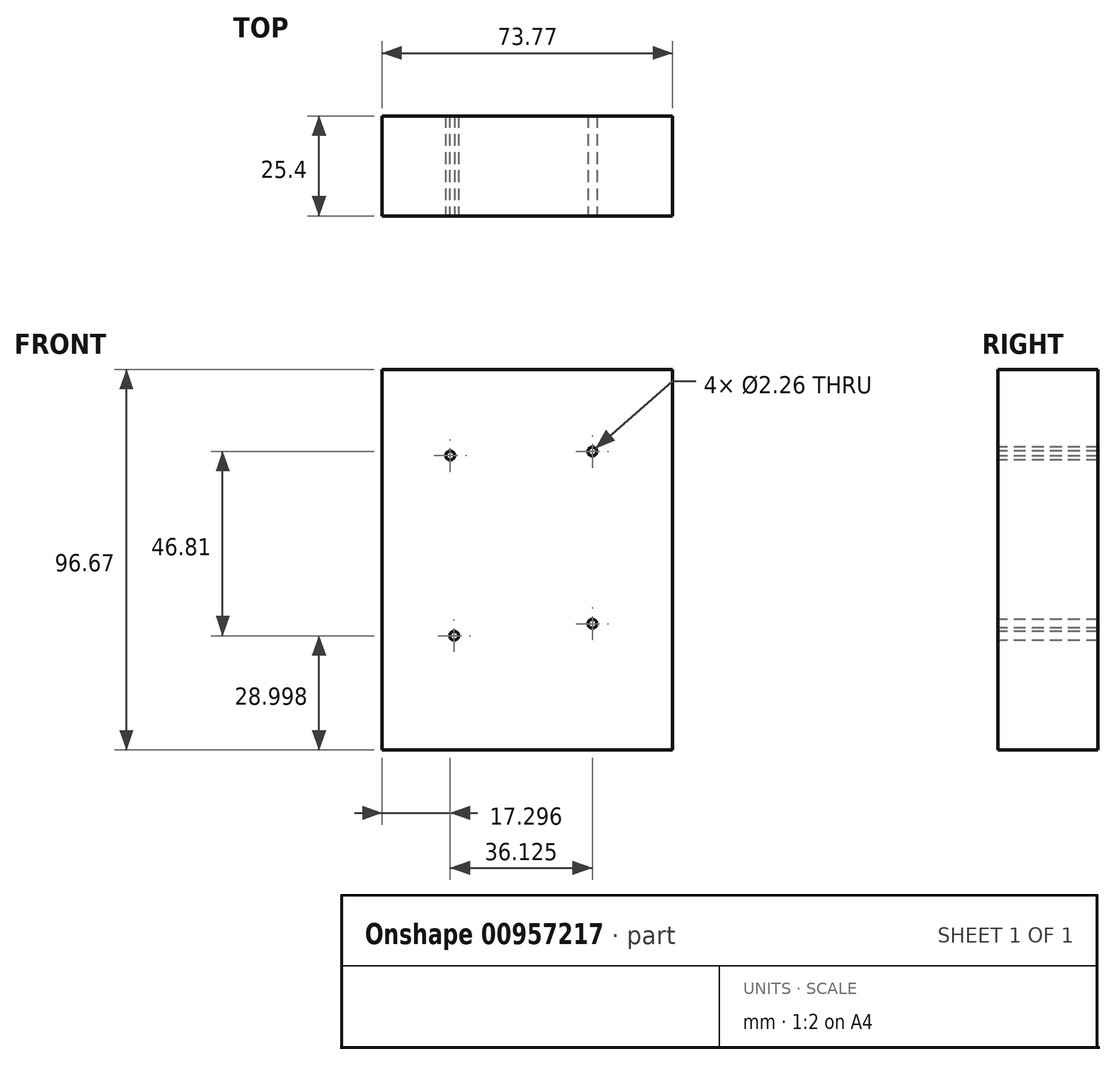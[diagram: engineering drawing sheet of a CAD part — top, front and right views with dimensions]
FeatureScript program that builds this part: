
annotation { "Feature Type Name" : "Feature", "Feature Type Description" : "" }
export const myFeature = defineFeature(function(context is Context, id is Id, definition is map)
    precondition{}
    {
        {
            var Q0;
            Q0=qCreatedBy(makeId("Front.planeOp"),FACE);
            var sketch = newSketch(context, id + "F0", { "sketchPlane" : qUnion([Q0])});
            skLineSegment(sketch, "E0.bottom", {"start": v(-29.38, 49.1) * mm, "end": v(44.4, 49.1) * mm});
            skLineSegment(sketch, "E0.top", {"start": v(-29.38, -47.57) * mm, "end": v(44.4, -47.57) * mm});
            skLineSegment(sketch, "E0.left", {"start": v(-29.38, 49.1) * mm, "end": v(-29.38, -47.57) * mm});
            skLineSegment(sketch, "E0.right", {"start": v(44.4, 49.1) * mm, "end": v(44.4, -47.57) * mm});
            skSolve(sketch);
        }
        {
            var Q0;
            Q0=makeQuery(id+"F0.imprint","IMPRINT",FACE,{"disambiguationData":[TD([[makeQuery(id+"F0.imprint","IMPRINT",EDGE,{"derivedFrom":sQuery(id+"F0.wireOp",EDGE,"E0.bottom")}),-1.0]])]});
            extrude(context, id + "F1", {"entities" : qUnion([Q0]), "depth" : 25.4 * mm, "offsetDistance" : 25.4 * mm});
        }
        {
            var Q0;
            Q0=makeQuery(id+"F1.opExtrude","CAP_FACE",FACE,{"disambiguationData":[OSD([sQuery(id+"F0.wireOp",EDGE,"E0.bottom"),sQuery(id+"F0.wireOp",EDGE,"E0.top"),sQuery(id+"F0.wireOp",EDGE,"E0.left"),sQuery(id+"F0.wireOp",EDGE,"E0.right")])],"isStart":false});
            var sketch = newSketch(context, id + "F2", { "sketchPlane" : qUnion([Q0])});
            skLineSegment(sketch, "E1", {"start": v(-12.08, 27.22) * mm, "end": v(24.04, -15.52) * mm});
            skLineSegment(sketch, "E2", {"start": v(24.04, 28.24) * mm, "end": v(-11.07, -18.57) * mm});
            skSolve(sketch);
        }
        {
            var Q0;
            Q0=sQuery(id+"F2.wireOp",VERTEX,"E1.start");
            var Q1;
            Q1=sQuery(id+"F2.wireOp",VERTEX,"E2.start");
            var Q2;
            Q2=sQuery(id+"F2.wireOp",VERTEX,"E2.end");
            var Q3;
            Q3=sQuery(id+"F2.wireOp",VERTEX,"E1.end");
            var Q4;
            Q4=makeQuery(id+"F1.opExtrude","SWEPT_BODY",BODY,{"disambiguationData":[OSD([sQuery(id+"F0.wireOp",EDGE,"E0.bottom"),sQuery(id+"F0.wireOp",EDGE,"E0.top"),sQuery(id+"F0.wireOp",EDGE,"E0.left"),sQuery(id+"F0.wireOp",EDGE,"E0.right")])]});
            hole(context, id + "F3", {"style" : HoleStyle.SIMPLE, "endStyle" : HoleEndStyle.THROUGH, "standardTappedOrClearance" : lookupTablePath({ "standard" : "ANSI", "engagement" : "75%", "pitch" : "40 tpi", "size" : "#4", "type" : "Tapped" }), "standardBlindInLast" : lookupTablePath({ "standard" : "ANSI", "fit" : "Normal", "engagement" : "75%", "pitch" : "40 tpi", "size" : "#4", "type" : "Clearance & tapped" }), "holeDiameter" : 2.26 * mm, "majorDiameter" : 2.84 * mm, "showTappedDepth" : true, "isTappedThrough" : true, "tappedDepth" : 3.96 * mm, "tapClearance" : 3, "locations" : qUnion([Q0, Q1, Q2, Q3]), "scope" : qUnion([Q4])});
        }
    });
